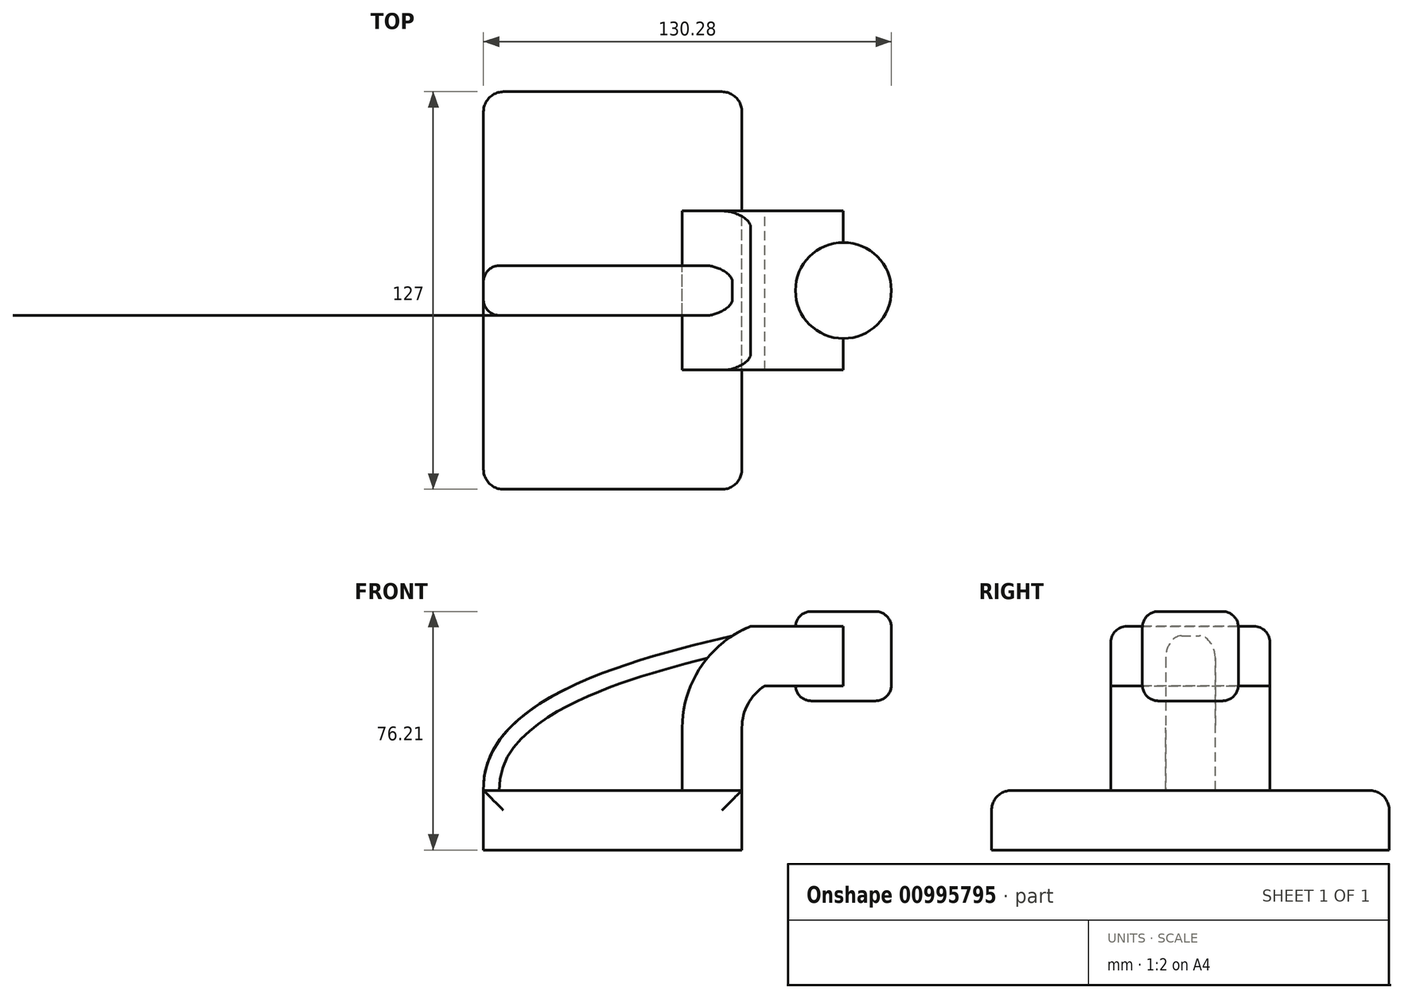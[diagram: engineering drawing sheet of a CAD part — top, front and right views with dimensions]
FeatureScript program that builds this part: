
annotation { "Feature Type Name" : "Feature", "Feature Type Description" : "" }
export const myFeature = defineFeature(function(context is Context, id is Id, definition is map)
    precondition{}
    {
        {
            var Q0;
            Q0=qCreatedBy(makeId("Front.planeOp"),FACE);
            var sketch = newSketch(context, id + "F0", { "sketchPlane" : qUnion([Q0])});
            skLineSegment(sketch, "E0.bottom", {"start": v(-41.28, -9.53) * mm, "end": v(41.28, -9.53) * mm});
            skLineSegment(sketch, "E0.top", {"start": v(-41.28, 9.53) * mm, "end": v(41.28, 9.53) * mm});
            skLineSegment(sketch, "E0.left", {"start": v(-41.28, -9.53) * mm, "end": v(-41.28, 9.53) * mm});
            skLineSegment(sketch, "E0.right", {"start": v(41.28, -9.53) * mm, "end": v(41.28, 9.53) * mm});
            skPoint(sketch, "E0.middle", {"position": v(0, 0) * mm});
            skLineSegment(sketch, "E1.bottom", {"start": v(89, 38.1) * mm, "end": v(38.2, 38.1) * mm});
            skLineSegment(sketch, "E1.top", {"start": v(89, 66.67) * mm, "end": v(38.2, 66.67) * mm});
            skLineSegment(sketch, "E1.left", {"start": v(89, 38.1) * mm, "end": v(89, 66.67) * mm});
            skLineSegment(sketch, "E1.right", {"start": v(38.2, 38.1) * mm, "end": v(38.2, 66.67) * mm});
            skPoint(sketch, "E1.middle", {"position": v(63.6, 52.39) * mm});
            skLineSegment(sketch, "E2", {"start": v(41.28, 9.53) * mm, "end": v(41.28, 29.54) * mm});
            skArc(sketch, "E3", {"start": v(41.28, 29.54) * mm, "mid": v(43.2, 37.13) * mm, "end": v(48.53, 42.88) * mm});
            skLineSegment(sketch, "E4", {"start": v(48.53, 42.88) * mm, "end": v(74.03, 42.88) * mm});
            skLineSegment(sketch, "E5.0", {"start": v(44.07, 61.93) * mm, "end": v(74.03, 61.93) * mm});
            skArc(sketch, "E5.1", {"start": v(22.23, 29.54) * mm, "mid": v(28.2, 49.07) * mm, "end": v(44.07, 61.93) * mm});
            skLineSegment(sketch, "E5.2", {"start": v(22.23, 9.53) * mm, "end": v(22.23, 29.54) * mm});
            skLineSegment(sketch, "E6", {"start": v(73.67, 38.1) * mm, "end": v(73.67, 66.67) * mm});
            skFitSpline(sketch, "E7", {"points": [v(-41.28, 9.53) * mm, v(38.2, 58.88) * mm], "startDerivative": vector(-1.94, 83.4) * mm, "endDerivative": vector(114.6, 26.38) * mm});
            skSolve(sketch);
        }
        {
            var Q0;
            Q0=makeQuery(id+"F0.imprint","IMPRINT",FACE,{"disambiguationData":[TD([[makeQuery(id+"F0.imprint","IMPRINT",EDGE,{"derivedFrom":sQuery(id+"F0.wireOp",EDGE,"E0.bottom")}),1.0]])]});
            extrude(context, id + "F1", {"entities" : qUnion([Q0]), "endBound" : BoundingType.SYMMETRIC, "depth" : 127 * mm, "offsetDistance" : 25.4 * mm});
        }
        {
            var Q0;
            {var subQ2=sQuery(id+"F0.wireOp",EDGE,"E5.2");Q0=makeQuery(id+"F0.imprint","IMPRINT",FACE,{"disambiguationData":[TD([[makeQuery(id+"F0.imprint","IMPRINT",EDGE,{"derivedFrom":subQ2}),1.0]])]});}
            extrude(context, id + "F2", {"entities" : qUnion([Q0]), "endBound" : BoundingType.SYMMETRIC, "depth" : 15.88 * mm, "offsetDistance" : 25.4 * mm});
        }
        {
            var Q0;
            {var subQ0=sQuery(id+"F0.wireOp",EDGE,"E2");Q0=makeQuery(id+"F0.imprint","IMPRINT",FACE,{"disambiguationData":[TD([[makeQuery(id+"F0.imprint","IMPRINT",EDGE,{"derivedFrom":subQ0}),1.0]])]});}
            var Q1;
            {var subQ3=sQuery(id+"F0.wireOp",EDGE,"E1.bottom");var subQ7=sQuery(id+"F0.wireOp",EDGE,"E1.right");var subQ8=makeQuery(id+"F0.imprint","INTERSECT",VERTEX,{"derivedFrom":[subQ3,subQ7]});Q1=makeQuery(id+"F0.imprint","IMPRINT",FACE,{"disambiguationData":[TD([[makeQuery(id+"F0.imprint","IMPRINT",EDGE,{"disambiguationData":[TD([[subQ8,1.0]])],"derivedFrom":subQ3}),-1.0]])]});}
            extrude(context, id + "F3", {"entities" : qUnion([Q0, Q1]), "endBound" : BoundingType.SYMMETRIC, "depth" : 50.8 * mm, "offsetDistance" : 25.4 * mm});
        }
        {
            var Q0;
            {var subQ4=sQuery(id+"F0.wireOp",EDGE,"E1.left");Q0=makeQuery(id+"F0.imprint","IMPRINT",FACE,{"disambiguationData":[TD([[makeQuery(id+"F0.imprint","IMPRINT",EDGE,{"derivedFrom":subQ4}),1.0]])]});}
            var Q1;
            Q1=sQuery(id+"F0.wireOp",EDGE,"E6");
            revolve(context, id + "F4", {"operationType" : NewBodyOperationType.ADD, "surfaceOperationType" : NewSurfaceOperationType.NEW, "entities" : qUnion([Q0]), "axis" : qUnion([Q1]), "revolveType" : RevolveType.FULL});
        }
        {
            var Q0;
            Q0=makeQuery(id+"F1.opExtrude","CAP_EDGE",EDGE,{"disambiguationData":[OSD([sQuery(id+"F0.wireOp",EDGE,"E0.left")])],"isStart":false});
            var Q1;
            Q1=makeQuery(id+"F1.opExtrude","CAP_EDGE",EDGE,{"disambiguationData":[OSD([sQuery(id+"F0.wireOp",EDGE,"E0.right")])],"isStart":false});
            var Q2;
            Q2=makeQuery(id+"F1.opExtrude","CAP_EDGE",EDGE,{"disambiguationData":[OSD([sQuery(id+"F0.wireOp",EDGE,"E0.right")])],"isStart":true});
            var Q3;
            Q3=makeQuery(id+"F1.opExtrude","CAP_EDGE",EDGE,{"disambiguationData":[OSD([sQuery(id+"F0.wireOp",EDGE,"E0.left")])],"isStart":true});
            var Q4;
            Q4=makeQuery(id+"F1.opExtrude","CAP_EDGE",EDGE,{"disambiguationData":[OSD([sQuery(id+"F0.wireOp",EDGE,"E0.top")])],"isStart":true});
            var Q5;
            Q5=makeQuery(id+"F1.opExtrude","CAP_EDGE",EDGE,{"disambiguationData":[OSD([sQuery(id+"F0.wireOp",EDGE,"E0.top")])],"isStart":false});
            fillet(context, id + "F5", {"entities" : qUnion([Q0, Q1, Q2, Q3, Q4, Q5]), "radius" : 6.35 * mm, "tangentPropagation" : true, "allowEdgeOverflow" : false});
        }
        {
            var Q0;
            Q0=makeQuery(id+"F4.opRevolve","SWEPT_EDGE",EDGE,{"disambiguationData":[OSD([sQuery(id+"F0.wireOp",EDGE,"E1.bottom"),sQuery(id+"F0.wireOp",EDGE,"E1.left")])]});
            var Q1;
            Q1=makeQuery(id+"F4.opRevolve","SWEPT_EDGE",EDGE,{"disambiguationData":[OSD([sQuery(id+"F0.wireOp",EDGE,"E1.top"),sQuery(id+"F0.wireOp",EDGE,"E1.left")])]});
            var Q2;
            Q2=makeQuery(id+"F2.opExtrude","CAP_EDGE",EDGE,{"disambiguationData":[OSD([sQuery(id+"F0.wireOp",EDGE,"E7")])],"isStart":false});
            var Q3;
            Q3=makeQuery(id+"F2.opExtrude","CAP_EDGE",EDGE,{"disambiguationData":[OSD([sQuery(id+"F0.wireOp",EDGE,"E7")])],"isStart":true});
            var Q4;
            Q4=makeQuery(id+"F3.opExtrude","CAP_EDGE",EDGE,{"disambiguationData":[OSD([sQuery(id+"F0.wireOp",EDGE,"E5.0")])],"isStart":false});
            var Q5;
            Q5=makeQuery(id+"F3.opExtrude","CAP_EDGE",EDGE,{"disambiguationData":[OSD([sQuery(id+"F0.wireOp",EDGE,"E5.0")])],"isStart":true});
            fillet(context, id + "F6", {"entities" : qUnion([Q0, Q1, Q2, Q3, Q4, Q5]), "radius" : 5.08 * mm, "tangentPropagation" : true, "allowEdgeOverflow" : false});
        }
    });
